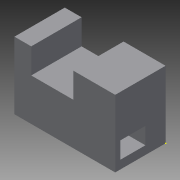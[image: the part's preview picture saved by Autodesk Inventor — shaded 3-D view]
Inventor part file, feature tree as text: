
AUTODESK INVENTOR PART (.ipt)
format: ipt  version: 2015 (Build 190159000, 159)  size: 88,576 bytes
history: native  units: in
note: dims shown in document units (in); Inventor stores cm internally (conversion verified against a paired STEP export)
features: sketch x3, extrude x2
ambient origin geometry x8: Origin, YZ Plane, XZ Plane, XY Plane, X Axis, Y Axis, Z Axis, Center Point
bodies: Solid1 (feature_tree)
feature tree (5):
  extrude  "Extrusion1"  Depth=60.0in
  sketch  "Sketch2"  dims[d2=40.0in d3=15.0in]
  extrude  "Extrusion2"  Depth=15.0in
  sketch  "Sketch1"  dims[d0=40.0in d1=60.0in]
  sketch  "Sketch3"  dims[d4=10.0in d5=25.0in d6=30.0in d7=0.0in d8=15.0in d9=10.0in d10=95.125in d11=0.0in]
